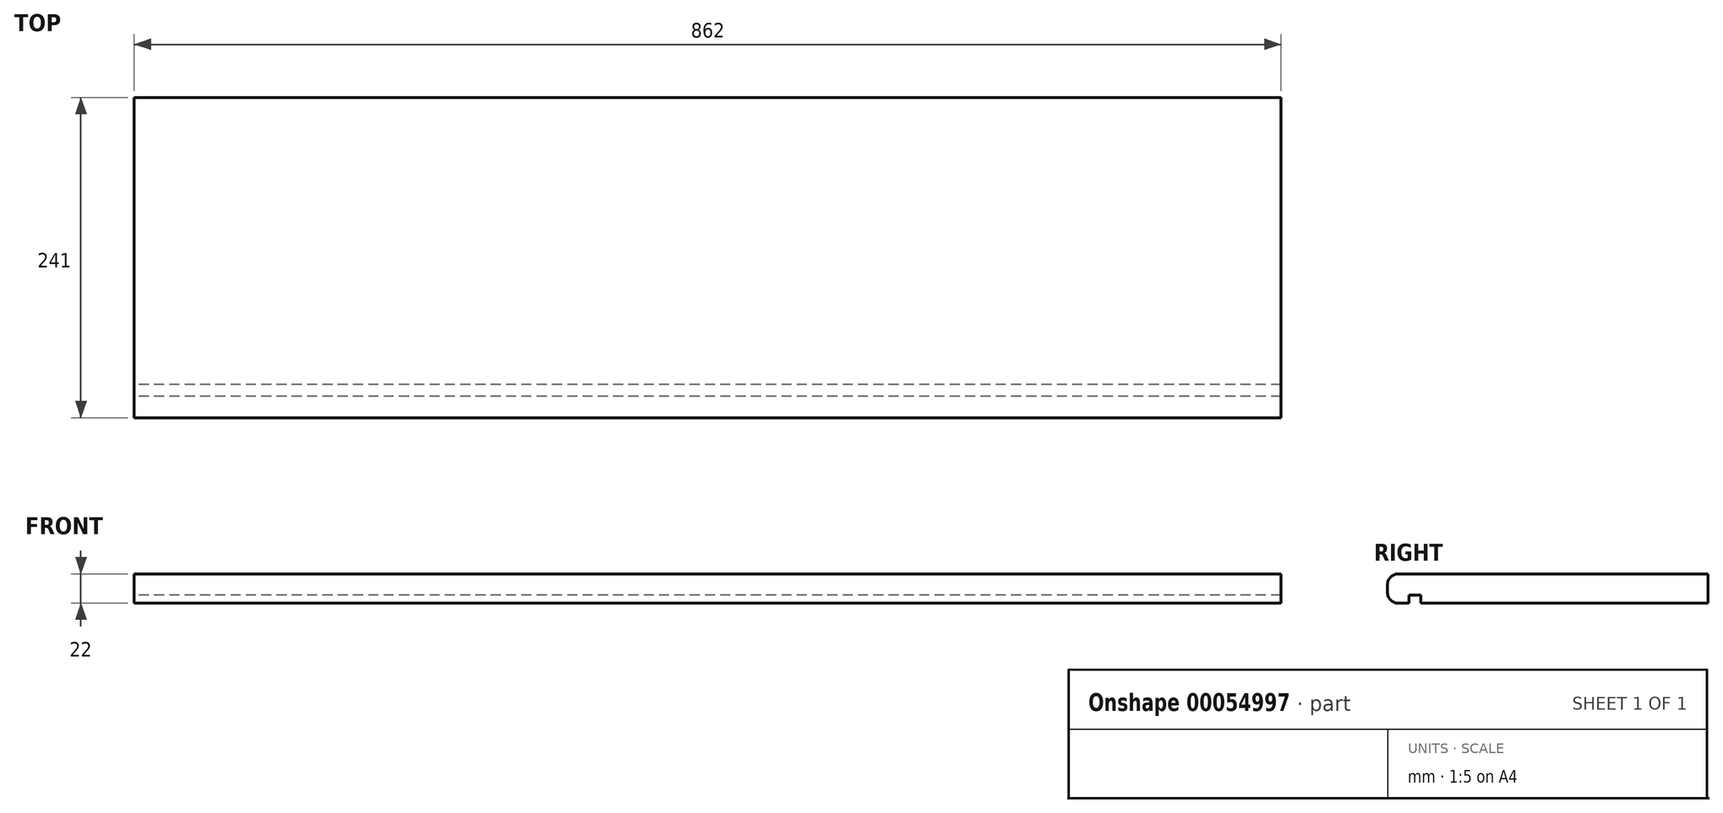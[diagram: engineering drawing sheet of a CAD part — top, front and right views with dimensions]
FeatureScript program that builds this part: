
annotation { "Feature Type Name" : "Feature", "Feature Type Description" : "" }
export const myFeature = defineFeature(function(context is Context, id is Id, definition is map)
    precondition{}
    {
        {
            var Q0;
            Q0=qCreatedBy(makeId("Right.planeOp"),FACE);
            var sketch = newSketch(context, id + "F0", { "sketchPlane" : qUnion([Q0])});
            skLineSegment(sketch, "E0.bottom", {"start": v(-115.68, 35.13) * mm, "end": v(117.32, 35.13) * mm});
            skLineSegment(sketch, "E0.top", {"start": v(-115.68, 13.13) * mm, "end": v(-107.68, 13.13) * mm});
            skLineSegment(sketch, "E0.left", {"start": v(-123.68, 27.13) * mm, "end": v(-123.68, 21.13) * mm});
            skLineSegment(sketch, "E0.right", {"start": v(117.32, 35.13) * mm, "end": v(117.32, 13.13) * mm});
            skLineSegment(sketch, "E1.top", {"start": v(-107.68, 19.13) * mm, "end": v(-97.68, 19.13) * mm});
            skLineSegment(sketch, "E1.left", {"start": v(-107.68, 13.13) * mm, "end": v(-107.68, 19.13) * mm});
            skLineSegment(sketch, "E1.right", {"start": v(-97.68, 13.13) * mm, "end": v(-97.68, 19.13) * mm});
            skLineSegment(sketch, "E2.trimOffspring", {"start": v(-97.68, 13.13) * mm, "end": v(117.32, 13.13) * mm});
            skPoint(sketch, "E3.visualSharp", {"position": v(-123.68, 35.13) * mm});
            skArc(sketch, "E3.filletArc", {"start": v(-115.68, 35.13) * mm, "mid": v(-121.33, 32.8) * mm, "end": v(-123.68, 27.13) * mm});
            skPoint(sketch, "E4.visualSharp", {"position": v(-123.68, 13.13) * mm});
            skArc(sketch, "E4.filletArc", {"start": v(-123.68, 21.13) * mm, "mid": v(-121.33, 15.48) * mm, "end": v(-115.68, 13.13) * mm});
            skSolve(sketch);
        }
        {
            var Q0;
            Q0 = qSketchRegion(id + "F0", true);
            extrude(context, id + "F1", {"entities" : qUnion([Q0]), "depth" : (900 - 64 + 26) * mm});
        }
        {
            var Q0;
            Q0=makeQuery(id+"F1.opExtrude","SWEPT_FACE",FACE,{"disambiguationData":[OSD([sQuery(id+"F0.wireOp",EDGE,"E1.right")])]});
            extrude(context, id + "F2", {"entities" : qUnion([Q0]), "operationType" : NewBodyOperationType.ADD, "depth" : 1 * mm});
        }
    });
